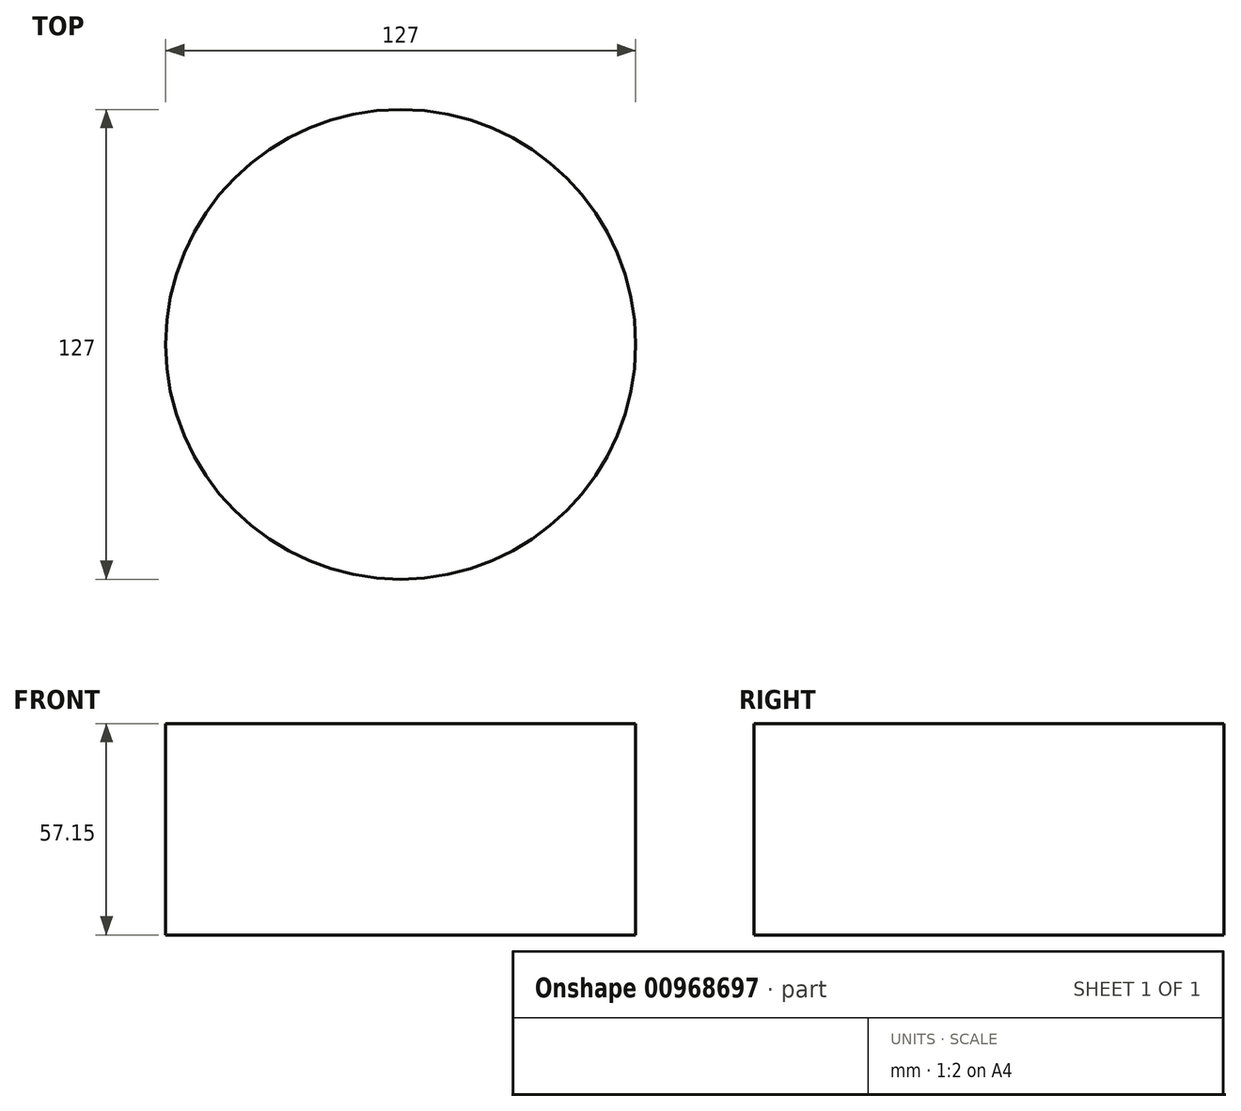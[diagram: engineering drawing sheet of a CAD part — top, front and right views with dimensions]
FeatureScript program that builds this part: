
annotation { "Feature Type Name" : "Feature", "Feature Type Description" : "" }
export const myFeature = defineFeature(function(context is Context, id is Id, definition is map)
    precondition{}
    {
        {
            var Q0;
            Q0=qCreatedBy(makeId("Top.planeOp"),FACE);
            var sketch = newSketch(context, id + "F0", { "sketchPlane" : qUnion([Q0])});
            skCircle(sketch, "E0", {"center": v(0, 0) * mm, "radius": 63.5 * mm});
            skSolve(sketch);
        }
        {
            var Q0;
            Q0=makeQuery(id+"F0.imprint","IMPRINT",FACE,{"disambiguationData":[TD([[makeQuery(id+"F0.imprint","IMPRINT",EDGE,{"derivedFrom":sQuery(id+"F0.wireOp",EDGE,"E0")}),1.0]])]});
            extrude(context, id + "F1", {"entities" : qUnion([Q0]), "depth" : 57.15 * mm, "offsetDistance" : 25.4 * mm});
        }
    });
